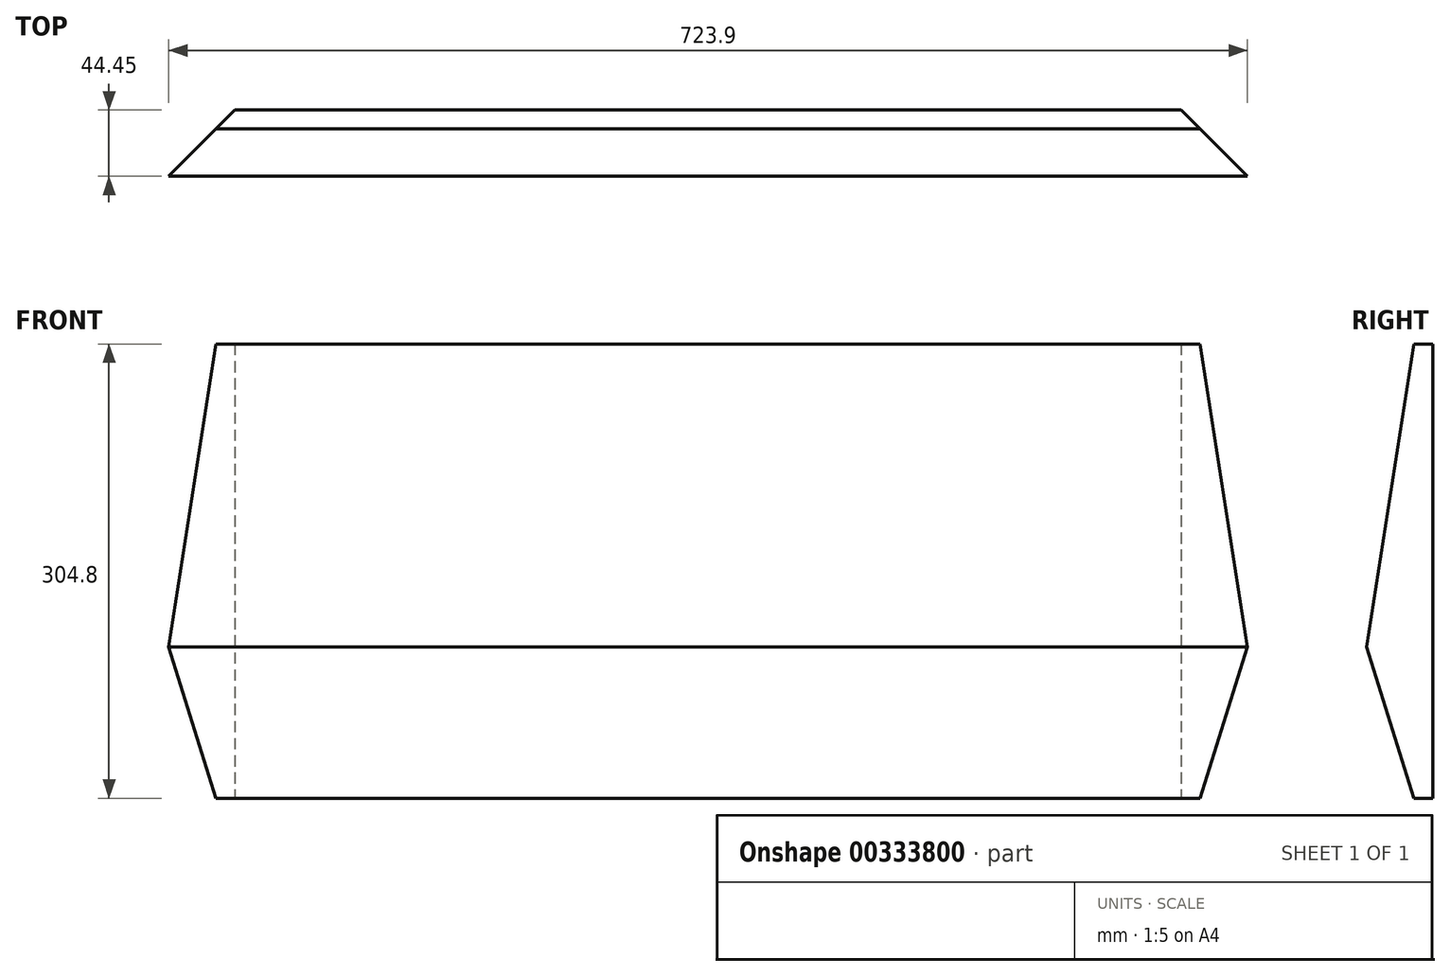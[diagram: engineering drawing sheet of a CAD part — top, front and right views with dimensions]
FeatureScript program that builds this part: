
annotation { "Feature Type Name" : "Feature", "Feature Type Description" : "" }
export const myFeature = defineFeature(function(context is Context, id is Id, definition is map)
    precondition{}
    {
        {
            var Q0;
            Q0=qCreatedBy(makeId("Front.planeOp"),FACE);
            var sketch = newSketch(context, id + "F0", { "sketchPlane" : qUnion([Q0])});
            skLineSegment(sketch, "E0.bottom", {"start": v(-74.09, 0) * mm, "end": v(662.51, 0) * mm});
            skLineSegment(sketch, "E0.top", {"start": v(-74.09, 304.8) * mm, "end": v(662.51, 304.8) * mm});
            skLineSegment(sketch, "E0.left", {"start": v(-74.09, 0) * mm, "end": v(-74.09, 304.8) * mm});
            skLineSegment(sketch, "E0.right", {"start": v(662.51, 0) * mm, "end": v(662.51, 304.8) * mm});
            skSolve(sketch);
        }
        {
            var Q0;
            Q0 = qSketchRegion(id + "F0", true);
            extrude(context, id + "F1", {"entities" : qUnion([Q0]), "depth" : 44.45 * mm});
        }
        {
            var Q0;
            Q0=makeQuery(id+"F1.opExtrude","SWEPT_FACE",FACE,{"disambiguationData":[OSD([sQuery(id+"F0.wireOp",EDGE,"E0.right")])]});
            var sketch = newSketch(context, id + "F2", { "sketchPlane" : qUnion([Q0])});
            skLineSegment(sketch, "E1", {"start": v(-12.7, 304.8) * mm, "end": v(-44.45, 101.6) * mm});
            skLineSegment(sketch, "E2", {"start": v(-82.84, 0) * mm, "end": v(-82.84, 304.8) * mm});
            skPoint(sketch, "E2.endSnap0", {"position": v(-22.23, 304.8) * mm});
            skLineSegment(sketch, "E3", {"start": v(-82.84, 304.8) * mm, "end": v(-12.7, 304.8) * mm});
            skLineSegment(sketch, "E4", {"start": v(-44.45, 101.6) * mm, "end": v(-12.7, 0) * mm});
            skLineSegment(sketch, "E5", {"start": v(-12.7, 0) * mm, "end": v(-82.84, 0) * mm});
            skSolve(sketch);
        }
        {
            var Q0;
            Q0 = qSketchRegion(id + "F2", true);
            extrude(context, id + "F3", {"entities" : qUnion([Q0]), "operationType" : NewBodyOperationType.REMOVE, "endBound" : BoundingType.THROUGH_ALL, "oppositeDirection" : true, "depth" : 25.4 * mm});
        }
        {
            var Q0;
            Q0=makeQuery(id+"F1.opExtrude","SWEPT_FACE",FACE,{"disambiguationData":[OSD([sQuery(id+"F0.wireOp",EDGE,"E0.bottom")])]});
            var sketch = newSketch(context, id + "F4", { "sketchPlane" : qUnion([Q0])});
            skLineSegment(sketch, "E6", {"start": v(662.51, 50.8) * mm, "end": v(662.51, 0) * mm});
            skLineSegment(sketch, "E7", {"start": v(662.51, 0) * mm, "end": v(611.71, 0) * mm});
            skLineSegment(sketch, "E8", {"start": v(611.71, 0) * mm, "end": v(662.51, 50.8) * mm});
            skLineSegment(sketch, "E9", {"start": v(294.21, 0) * mm, "end": v(294.21, 75.38) * mm, "construction": true});
            skPoint(sketch, "E9.endSnap0", {"position": v(294.21, 12.7) * mm});
            skLineSegment(sketch, "E10.MirrorCS", {"start": v(-74.09, 50.8) * mm, "end": v(-74.09, 0) * mm});
            skLineSegment(sketch, "E11.MirrorCS", {"start": v(-74.09, 0) * mm, "end": v(-23.29, 0) * mm});
            skLineSegment(sketch, "E12.MirrorCS", {"start": v(-23.29, 0) * mm, "end": v(-74.09, 50.8) * mm});
            skSolve(sketch);
        }
        {
            var Q0;
            Q0 = qSketchRegion(id + "F4", true);
            extrude(context, id + "F5", {"entities" : qUnion([Q0]), "operationType" : NewBodyOperationType.REMOVE, "endBound" : BoundingType.THROUGH_ALL, "oppositeDirection" : true, "depth" : 25.4 * mm});
        }
    });
